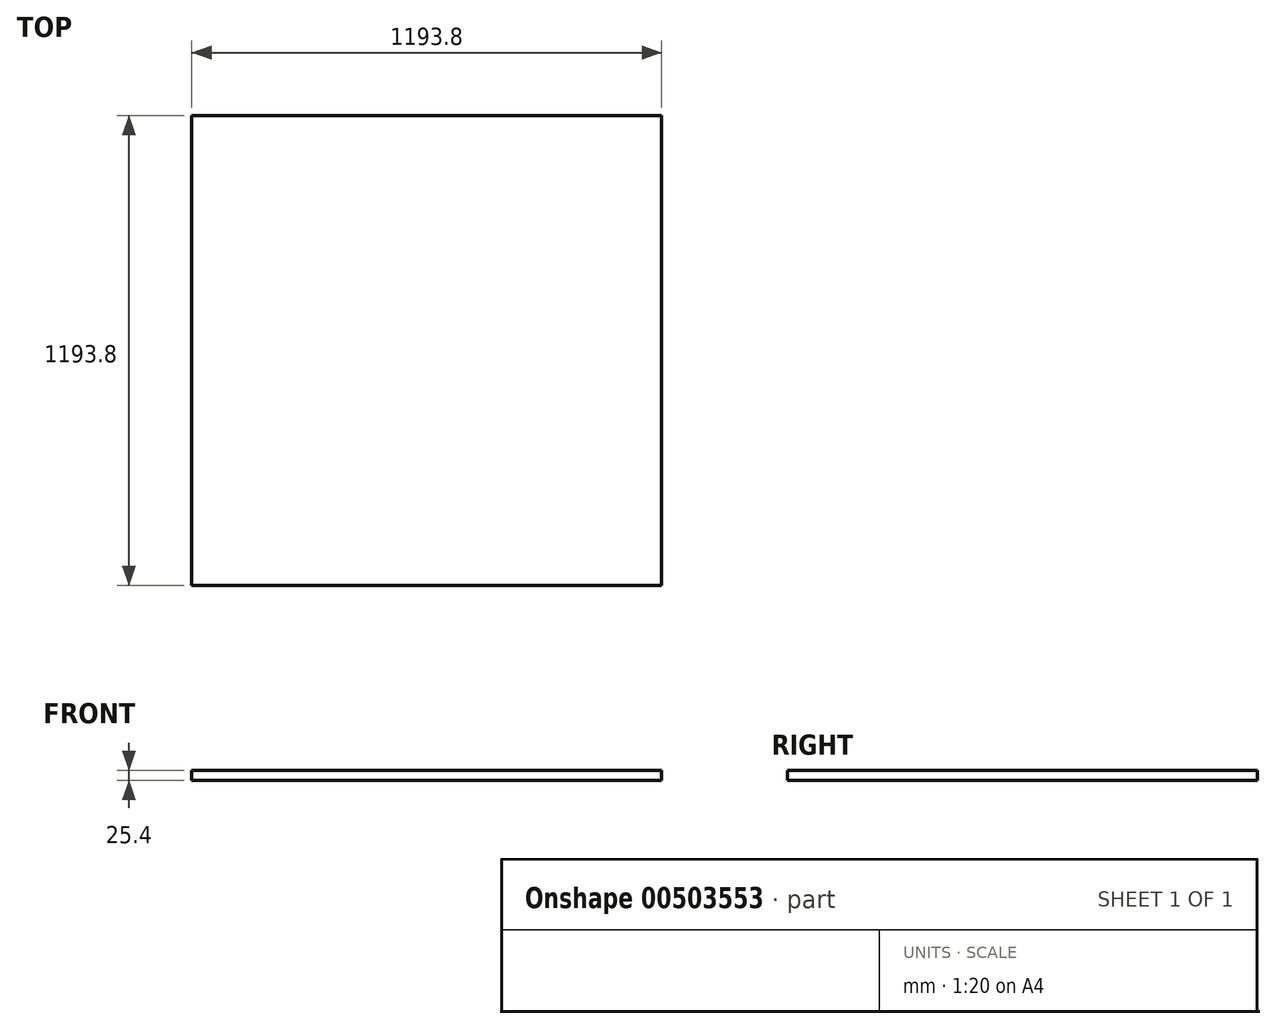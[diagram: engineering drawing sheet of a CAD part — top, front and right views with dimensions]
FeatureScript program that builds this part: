
annotation { "Feature Type Name" : "Feature", "Feature Type Description" : "" }
export const myFeature = defineFeature(function(context is Context, id is Id, definition is map)
    precondition{}
    {
        {
            var Q0;
            Q0=qCreatedBy(makeId("Top.planeOp"),FACE);
            var sketch = newSketch(context, id + "F0", { "sketchPlane" : qUnion([Q0])});
            skLineSegment(sketch, "E0.bottom", {"start": v(596.9, 596.9) * mm, "end": v(-596.9, 596.9) * mm});
            skLineSegment(sketch, "E0.top", {"start": v(596.9, -596.9) * mm, "end": v(-596.9, -596.9) * mm});
            skLineSegment(sketch, "E0.left", {"start": v(596.9, 596.9) * mm, "end": v(596.9, -596.9) * mm});
            skLineSegment(sketch, "E0.right", {"start": v(-596.9, 596.9) * mm, "end": v(-596.9, -596.9) * mm});
            skPoint(sketch, "E0.middle", {"position": v(0, 0) * mm});
            skSolve(sketch);
        }
        {
            var Q0;
            Q0=makeQuery(id+"F0.imprint","IMPRINT",FACE,{"disambiguationData":[TD([[makeQuery(id+"F0.imprint","IMPRINT",EDGE,{"derivedFrom":sQuery(id+"F0.wireOp",EDGE,"E0.bottom")}),1.0]])]});
            extrude(context, id + "F1", {"entities" : qUnion([Q0]), "endBound" : BoundingType.SYMMETRIC, "depth" : 25.4 * mm});
        }
    });
